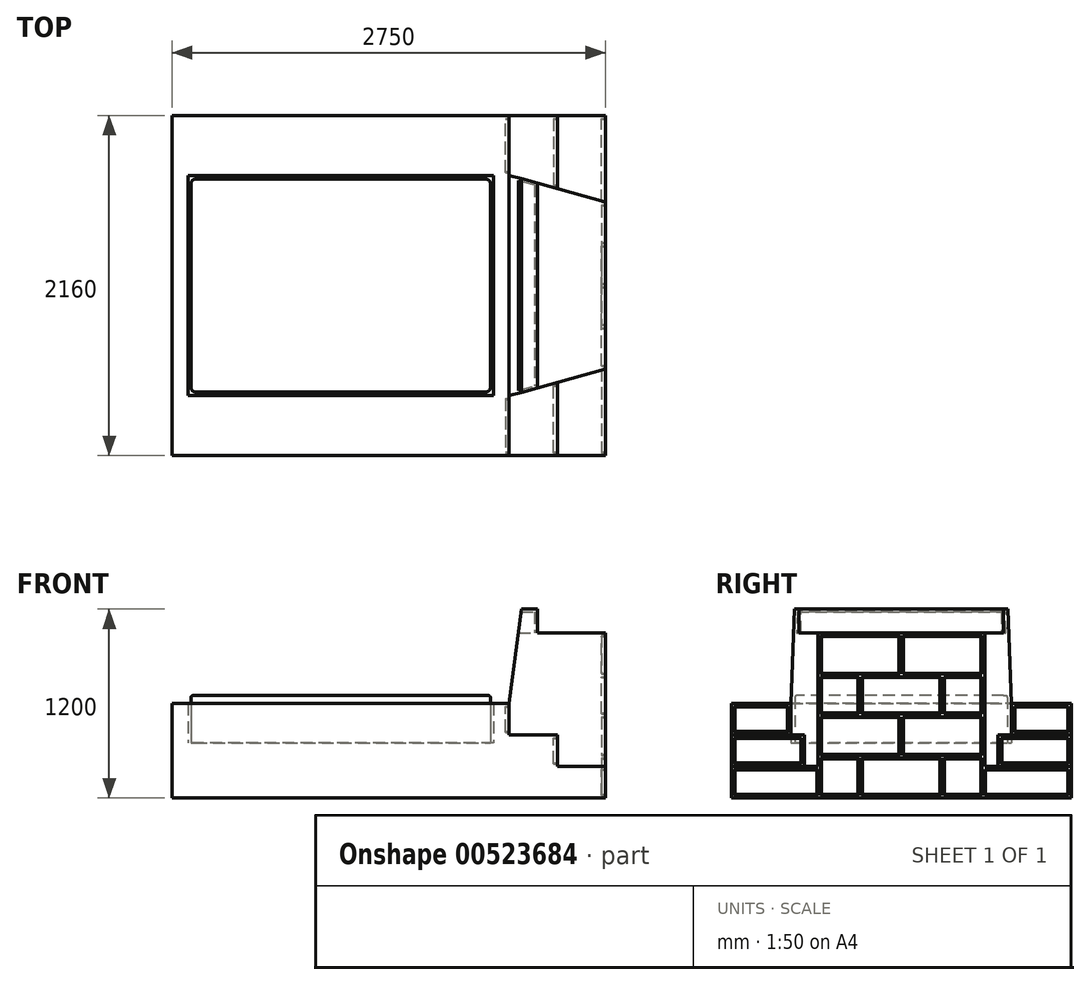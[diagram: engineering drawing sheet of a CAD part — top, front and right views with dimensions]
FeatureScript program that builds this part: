
annotation { "Feature Type Name" : "Feature", "Feature Type Description" : "" }
export const myFeature = defineFeature(function(context is Context, id is Id, definition is map)
    precondition{}
    {
        {
            var Q0;
            Q0=qCreatedBy(makeId("Top.planeOp"),FACE);
            var sketch = newSketch(context, id + "F0", { "sketchPlane" : qUnion([Q0])});
            skLineSegment(sketch, "E0.bottom", {"start": v(1572.5, 1080) * mm, "end": v(-1177.5, 1080) * mm});
            skLineSegment(sketch, "E0.top", {"start": v(1572.5, -1080) * mm, "end": v(-1177.5, -1080) * mm});
            skLineSegment(sketch, "E0.left", {"start": v(1572.5, 1080) * mm, "end": v(1572.5, -1080) * mm});
            skLineSegment(sketch, "E0.right", {"start": v(-1177.5, 1080) * mm, "end": v(-1177.5, -1080) * mm});
            skPoint(sketch, "E0.middle", {"position": v(197.5, 0) * mm});
            skLineSegment(sketch, "E1.bottom", {"start": v(862.5, -700) * mm, "end": v(-1077.5, -700) * mm});
            skLineSegment(sketch, "E1.top", {"start": v(862.5, 700) * mm, "end": v(-1077.5, 700) * mm});
            skLineSegment(sketch, "E1.left", {"start": v(862.5, -700) * mm, "end": v(862.5, 700) * mm});
            skLineSegment(sketch, "E1.right", {"start": v(-1077.5, -700) * mm, "end": v(-1077.5, 700) * mm});
            skPoint(sketch, "E1.middle", {"position": v(-107.5, 0) * mm});
            skLineSegment(sketch, "E2", {"start": v(962.5, 700) * mm, "end": v(962.5, -700) * mm});
            skSolve(sketch);
        }
        {
            var Q0;
            Q0=makeQuery(id+"F0.imprint","IMPRINT",FACE,{"disambiguationData":[TD([[makeQuery(id+"F0.imprint","IMPRINT",EDGE,{"derivedFrom":sQuery(id+"F0.wireOp",EDGE,"E0.bottom")}),1.0]])]});
            extrude(context, id + "F1", {"entities" : qUnion([Q0]), "depth" : 600 * mm, "offsetDistance" : 25 * mm});
        }
        {
            var Q0;
            Q0=makeQuery(id+"F1.opExtrude","CAP_FACE",FACE,{"disambiguationData":[OSD([sQuery(id+"F0.wireOp",EDGE,"E0.bottom"),sQuery(id+"F0.wireOp",EDGE,"E0.top"),sQuery(id+"F0.wireOp",EDGE,"E0.left"),sQuery(id+"F0.wireOp",EDGE,"E0.right"),sQuery(id+"F0.wireOp",EDGE,"E1.bottom"),sQuery(id+"F0.wireOp",EDGE,"E1.top"),sQuery(id+"F0.wireOp",EDGE,"E1.left"),sQuery(id+"F0.wireOp",EDGE,"E1.right")])],"isStart":false});
            var sketch = newSketch(context, id + "F2", { "sketchPlane" : qUnion([Q0])});
            skLineSegment(sketch, "E3", {"start": v(962.5, 1080) * mm, "end": v(962.5, -1080) * mm});
            skLineSegment(sketch, "E4", {"start": v(962.5, -700) * mm, "end": v(1572.5, -530) * mm});
            skLineSegment(sketch, "E5", {"start": v(962.5, 700) * mm, "end": v(1572.5, 530) * mm});
            skLineSegment(sketch, "E6", {"start": v(1267.5, -1080) * mm, "end": v(1267.5, -615) * mm});
            skPoint(sketch, "E6.startSnap0", {"position": v(1267.5, -615) * mm});
            skLineSegment(sketch, "E7", {"start": v(1267.5, 615) * mm, "end": v(1267.5, 1080) * mm});
            skSolve(sketch);
        }
        {
            var Q0;
            {var subQ5=sQuery(id+"F2.wireOp",EDGE,"E7");Q0=makeQuery(id+"F2.imprint","IMPRINT",FACE,{"disambiguationData":[TD([[makeQuery(id+"F2.imprint","IMPRINT",EDGE,{"derivedFrom":subQ5}),1.0]])]});}
            var Q1;
            {var subQ5=sQuery(id+"F2.wireOp",EDGE,"E6");Q1=makeQuery(id+"F2.imprint","IMPRINT",FACE,{"disambiguationData":[TD([[makeQuery(id+"F2.imprint","IMPRINT",EDGE,{"derivedFrom":subQ5}),1.0]])]});}
            extrude(context, id + "F3", {"entities" : qUnion([Q0, Q1]), "operationType" : NewBodyOperationType.REMOVE, "oppositeDirection" : true, "depth" : 200 * mm, "offsetDistance" : 25 * mm});
        }
        {
            var Q0;
            {var subQ3=sQuery(id+"F2.wireOp",EDGE,"E6");Q0=makeQuery(id+"F2.imprint","IMPRINT",FACE,{"disambiguationData":[TD([[makeQuery(id+"F2.imprint","IMPRINT",EDGE,{"derivedFrom":subQ3}),-1.0]])]});}
            var Q1;
            {var subQ3=sQuery(id+"F2.wireOp",EDGE,"E7");Q1=makeQuery(id+"F2.imprint","IMPRINT",FACE,{"disambiguationData":[TD([[makeQuery(id+"F2.imprint","IMPRINT",EDGE,{"derivedFrom":subQ3}),-1.0]])]});}
            extrude(context, id + "F4", {"entities" : qUnion([Q0, Q1]), "operationType" : NewBodyOperationType.REMOVE, "oppositeDirection" : true, "depth" : 400 * mm, "offsetDistance" : 25 * mm});
        }
        {
            var Q0;
            Q0=makeQuery(id+"F1.opExtrude","CAP_FACE",FACE,{"disambiguationData":[OSD([sQuery(id+"F0.wireOp",EDGE,"E0.bottom"),sQuery(id+"F0.wireOp",EDGE,"E0.top"),sQuery(id+"F0.wireOp",EDGE,"E0.left"),sQuery(id+"F0.wireOp",EDGE,"E0.right"),sQuery(id+"F0.wireOp",EDGE,"E1.bottom"),sQuery(id+"F0.wireOp",EDGE,"E1.top"),sQuery(id+"F0.wireOp",EDGE,"E1.left"),sQuery(id+"F0.wireOp",EDGE,"E1.right")])],"isStart":false});
            var sketch = newSketch(context, id + "F5", { "sketchPlane" : qUnion([Q0])});
            skLineSegment(sketch, "E8.0", {"start": v(1572.5, 530) * mm, "end": v(1572.5, -530) * mm});
            skLineSegment(sketch, "E9.0", {"start": v(962.5, 700) * mm, "end": v(1572.5, 530) * mm});
            skLineSegment(sketch, "E10.0", {"start": v(962.5, -700) * mm, "end": v(1572.5, -530) * mm});
            skLineSegment(sketch, "E11.0", {"start": v(862.5, -700) * mm, "end": v(862.5, 700) * mm});
            skLineSegment(sketch, "E12", {"start": v(962.5, 700) * mm, "end": v(962.5, -700) * mm});
            skSolve(sketch);
        }
        {
            var Q0;
            Q0=makeQuery(id+"F5.imprint","IMPRINT",FACE,{"disambiguationData":[TD([[makeQuery(id+"F5.imprint","IMPRINT",EDGE,{"derivedFrom":sQuery(id+"F5.wireOp",EDGE,"E8.0")}),-1.0]])]});
            extrude(context, id + "F6", {"entities" : qUnion([Q0]), "operationType" : NewBodyOperationType.ADD, "depth" : 600 * mm, "offsetDistance" : 25 * mm});
        }
        {
            var Q0;
            Q0=makeQuery(id+"F6.opExtrude","CAP_FACE",FACE,{"disambiguationData":[OSD([sQuery(id+"F5.wireOp",EDGE,"E8.0"),sQuery(id+"F5.wireOp",EDGE,"E9.0"),sQuery(id+"F5.wireOp",EDGE,"E10.0"),sQuery(id+"F5.wireOp",EDGE,"E12")])],"isStart":false});
            var sketch = newSketch(context, id + "F7", { "sketchPlane" : qUnion([Q0])});
            skLineSegment(sketch, "E13.0", {"start": v(1041.49, 677.99) * mm, "end": v(1041.49, -677.99) * mm});
            skLineSegment(sketch, "E14.0", {"start": v(1041.49, -677.99) * mm, "end": v(1572.5, -530) * mm});
            skLineSegment(sketch, "E15.0", {"start": v(1041.49, 677.99) * mm, "end": v(1572.5, 530) * mm});
            skLineSegment(sketch, "E16.0", {"start": v(1572.5, 530) * mm, "end": v(1572.5, -530) * mm});
            skLineSegment(sketch, "E17", {"start": v(1141.49, -650.12) * mm, "end": v(1141.49, 650.12) * mm});
            skSolve(sketch);
        }
        {
            var Q0;
            {var subQ0=sQuery(id+"F7.wireOp",EDGE,"E16.0");Q0=makeQuery(id+"F7.imprint","IMPRINT",FACE,{"disambiguationData":[TD([[makeQuery(id+"F7.imprint","IMPRINT",EDGE,{"derivedFrom":subQ0}),-1.0]])]});}
            extrude(context, id + "F8", {"entities" : qUnion([Q0]), "operationType" : NewBodyOperationType.REMOVE, "oppositeDirection" : true, "depth" : 150 * mm, "offsetDistance" : 25 * mm});
        }
        {
            var Q0;
            Q0=makeQuery(id+"F6.boolean.opBoolean","MERGE",FACE,{"derivedFrom":[makeQuery(id+"F1.opExtrude","SWEPT_FACE",FACE,{"disambiguationData":[OSD([sQuery(id+"F0.wireOp",EDGE,"E0.left")])]}),makeQuery(id+"F6.opExtrude","SWEPT_FACE",FACE,{"disambiguationData":[OSD([sQuery(id+"F5.wireOp",EDGE,"E8.0")])]})]});
            var sketch = newSketch(context, id + "F9", { "sketchPlane" : qUnion([Q0])});
            skLineSegment(sketch, "E18.1", {"start": v(-512, 182) * mm, "end": v(-512, 1032) * mm});
            skLineSegment(sketch, "E18.2", {"start": v(-1062, 182) * mm, "end": v(-1062, 18) * mm});
            skLineSegment(sketch, "E18.3", {"start": v(512, 1032) * mm, "end": v(-512, 1032) * mm});
            skLineSegment(sketch, "E18.4", {"start": v(1062, 18) * mm, "end": v(-1062, 18) * mm});
            skLineSegment(sketch, "E18.5", {"start": v(1062, 182) * mm, "end": v(1062, 18) * mm});
            skLineSegment(sketch, "E18.6", {"start": v(1062, 182) * mm, "end": v(512, 182) * mm});
            skLineSegment(sketch, "E18.7", {"start": v(512, 182) * mm, "end": v(512, 1032) * mm});
            skLineSegment(sketch, "E19", {"start": v(-512, 182) * mm, "end": v(-512, 18) * mm});
            skLineSegment(sketch, "E20", {"start": v(512, 182) * mm, "end": v(512, 18) * mm});
            skLineSegment(sketch, "E21", {"start": v(512, 18) * mm, "end": v(530, 18) * mm});
            skLineSegment(sketch, "E22", {"start": v(530, 18) * mm, "end": v(530, 200) * mm});
            skLineSegment(sketch, "E23", {"start": v(-530, 18) * mm, "end": v(-530, 182) * mm});
            skLineSegment(sketch, "E24", {"start": v(-530, 182) * mm, "end": v(-1062, 182) * mm});
            skLineSegment(sketch, "E25.bottom", {"start": v(-535, 177) * mm, "end": v(-1057, 177) * mm});
            skLineSegment(sketch, "E25.top", {"start": v(-535, 23) * mm, "end": v(-1057, 23) * mm});
            skLineSegment(sketch, "E25.left", {"start": v(-535, 177) * mm, "end": v(-535, 23) * mm});
            skLineSegment(sketch, "E25.right", {"start": v(-1057, 177) * mm, "end": v(-1057, 23) * mm});
            skPoint(sketch, "E25.middle", {"position": v(-796, 100) * mm});
            skPoint(sketch, "E25.middle.positionSnap0", {"position": v(-796, 182) * mm});
            skPoint(sketch, "E25.middle.positionSnap1", {"position": v(-1062, 100) * mm});
            skPoint(sketch, "E25.centerSnap0", {"position": v(-796, 182) * mm});
            skPoint(sketch, "E25.centerSnap1", {"position": v(-1062, 100) * mm});
            skSolve(sketch);
        }
        {
            var Q0;
            {var subQ2=sQuery(id+"F9.wireOp",EDGE,"E18.2");Q0=makeQuery(id+"F9.imprint","IMPRINT",FACE,{"disambiguationData":[TD([[makeQuery(id+"F9.imprint","IMPRINT",EDGE,{"derivedFrom":subQ2}),1.0]])]});}
            extrude(context, id + "F10", {"entities" : qUnion([Q0]), "operationType" : NewBodyOperationType.REMOVE, "oppositeDirection" : true, "depth" : 25 * mm, "offsetDistance" : 25 * mm});
        }
        {
            var Q0;
            Q0=makeQuery(id+"F4.boolean.opBoolean","COPY",FACE,{"derivedFrom":makeQuery(id+"F4.opExtrude","SWEPT_FACE",FACE,{"disambiguationData":[OSD([sQuery(id+"F2.wireOp",EDGE,"E6")])]})});
            var sketch = newSketch(context, id + "F11", { "sketchPlane" : qUnion([Q0])});
            skLineSegment(sketch, "E26.0", {"start": v(-1062, 218) * mm, "end": v(-1062, 382) * mm});
            skLineSegment(sketch, "E26.1", {"start": v(-1062, 218) * mm, "end": v(-633, 218) * mm});
            skLineSegment(sketch, "E26.2", {"start": v(-633, 218) * mm, "end": v(-633, 382) * mm});
            skLineSegment(sketch, "E26.3", {"start": v(-1062, 382) * mm, "end": v(-633, 382) * mm});
            skLineSegment(sketch, "E27.0", {"start": v(-1057, 223) * mm, "end": v(-1057, 377) * mm});
            skLineSegment(sketch, "E27.1", {"start": v(-1057, 223) * mm, "end": v(-638, 223) * mm});
            skLineSegment(sketch, "E27.2", {"start": v(-638, 223) * mm, "end": v(-638, 377) * mm});
            skLineSegment(sketch, "E27.3", {"start": v(-1057, 377) * mm, "end": v(-638, 377) * mm});
            skSolve(sketch);
        }
        {
            var Q0;
            Q0 = qSketchRegion(id + "F11", true);
            extrude(context, id + "F12", {"entities" : qUnion([Q0]), "operationType" : NewBodyOperationType.REMOVE, "oppositeDirection" : true, "depth" : 25 * mm, "offsetDistance" : 25 * mm});
        }
        {
            var Q0;
            {var subQ0=sQuery(id+"F2.wireOp",EDGE,"E3");Q0=makeQuery(id+"F3.boolean.opBoolean","COPY",FACE,{"derivedFrom":makeQuery(id+"F3.opExtrude","SWEPT_FACE",FACE,{"disambiguationData":[OSD([subQ0]),TDD([makeQuery(id+"F2.imprint","IMPRINT",EDGE,{"disambiguationData":[TD([[makeQuery(id+"F2.imprint","INTERSECT",VERTEX,{"derivedFrom":[makeQuery(id+"F1.opExtrude","CAP_EDGE",EDGE,{"disambiguationData":[OSD([sQuery(id+"F0.wireOp",EDGE,"E0.top")])],"isStart":false}),subQ0]}),1.0]])],"derivedFrom":subQ0})])]})});}
            var sketch = newSketch(context, id + "F13", { "sketchPlane" : qUnion([Q0])});
            skLineSegment(sketch, "E28.0", {"start": v(-1062, 418) * mm, "end": v(-1062, 582) * mm});
            skLineSegment(sketch, "E28.1", {"start": v(-718, 418) * mm, "end": v(-1062, 418) * mm});
            skLineSegment(sketch, "E28.2", {"start": v(-718, 418) * mm, "end": v(-718, 582) * mm});
            skLineSegment(sketch, "E28.3", {"start": v(-718, 582) * mm, "end": v(-1062, 582) * mm});
            skLineSegment(sketch, "E29.0", {"start": v(-1057, 423) * mm, "end": v(-1057, 577) * mm});
            skLineSegment(sketch, "E29.1", {"start": v(-723, 423) * mm, "end": v(-1057, 423) * mm});
            skLineSegment(sketch, "E29.2", {"start": v(-723, 423) * mm, "end": v(-723, 577) * mm});
            skLineSegment(sketch, "E29.3", {"start": v(-723, 577) * mm, "end": v(-1057, 577) * mm});
            skSolve(sketch);
        }
        {
            var Q0;
            Q0 = qSketchRegion(id + "F13", true);
            extrude(context, id + "F14", {"entities" : qUnion([Q0]), "operationType" : NewBodyOperationType.REMOVE, "oppositeDirection" : true, "depth" : 25 * mm, "offsetDistance" : 25 * mm});
        }
        {
            var Q0;
            {var subQ1=sQuery(id+"F0.wireOp",EDGE,"E0.left");var subQ2=sQuery(id+"F0.wireOp",EDGE,"E0.bottom");Q0=makeQuery(id+"F10.boolean.opBoolean","SPLIT",FACE,{"disambiguationData":[TD([makeQuery(id+"F1.opExtrude","SWEPT_FACE",FACE,{"disambiguationData":[OSD([subQ2])]})])],"derivedFrom":makeQuery(id+"F6.boolean.opBoolean","MERGE",FACE,{"derivedFrom":[makeQuery(id+"F1.opExtrude","SWEPT_FACE",FACE,{"disambiguationData":[OSD([subQ1])]}),makeQuery(id+"F6.opExtrude","SWEPT_FACE",FACE,{"disambiguationData":[OSD([sQuery(id+"F5.wireOp",EDGE,"E8.0")])]})]})});}
            var sketch = newSketch(context, id + "F15", { "sketchPlane" : qUnion([Q0])});
            skLineSegment(sketch, "E30.bottom", {"start": v(-530, 1050) * mm, "end": v(530, 1050) * mm});
            skLineSegment(sketch, "E30.top", {"start": v(-530, 0) * mm, "end": v(530, 0) * mm});
            skLineSegment(sketch, "E30.left", {"start": v(-530, 1050) * mm, "end": v(-530, 0) * mm});
            skLineSegment(sketch, "E30.right", {"start": v(530, 1050) * mm, "end": v(530, 0) * mm});
            skLineSegment(sketch, "E31.0", {"start": v(512, 1032) * mm, "end": v(512, 18) * mm});
            skLineSegment(sketch, "E31.1", {"start": v(-512, 1032) * mm, "end": v(512, 1032) * mm});
            skLineSegment(sketch, "E31.2", {"start": v(-512, 1032) * mm, "end": v(-512, 18) * mm});
            skLineSegment(sketch, "E31.3", {"start": v(-512, 18) * mm, "end": v(512, 18) * mm});
            skLineSegment(sketch, "E32", {"start": v(0, 778.5) * mm, "end": v(512, 778.5) * mm});
            skLineSegment(sketch, "E33", {"start": v(0, 778.5) * mm, "end": v(0, 1032) * mm});
            skLineSegment(sketch, "E34", {"start": v(512, 1032) * mm, "end": v(512, 778.5) * mm});
            skLineSegment(sketch, "E35.0", {"start": v(9, 787.5) * mm, "end": v(512, 787.5) * mm});
            skLineSegment(sketch, "E35.1", {"start": v(9, 787.5) * mm, "end": v(9, 1032) * mm});
            skLineSegment(sketch, "E36.bottom", {"start": v(507, 792.5) * mm, "end": v(14, 792.5) * mm});
            skLineSegment(sketch, "E36.top", {"start": v(507, 1027) * mm, "end": v(14, 1027) * mm});
            skLineSegment(sketch, "E36.left", {"start": v(507, 792.5) * mm, "end": v(507, 1027) * mm});
            skLineSegment(sketch, "E36.right", {"start": v(14, 792.5) * mm, "end": v(14, 1027) * mm});
            skPoint(sketch, "E36.middle", {"position": v(260.5, 909.75) * mm});
            skPoint(sketch, "E36.middle.positionSnap0", {"position": v(260.5, 787.5) * mm});
            skPoint(sketch, "E36.middle.positionSnap1", {"position": v(9, 909.75) * mm});
            skPoint(sketch, "E36.centerSnap0", {"position": v(260.5, 787.5) * mm});
            skPoint(sketch, "E36.centerSnap1", {"position": v(9, 909.75) * mm});
            skLineSegment(sketch, "E37.MirrorCS", {"start": v(-9, 787.5) * mm, "end": v(-512, 787.5) * mm});
            skPoint(sketch, "E38.MirrorP", {"position": v(-260.5, 909.75) * mm});
            skLineSegment(sketch, "E39.MirrorCS", {"start": v(-507, 1027) * mm, "end": v(-14, 1027) * mm});
            skPoint(sketch, "E40.MirrorP", {"position": v(-260.5, 787.5) * mm});
            skLineSegment(sketch, "E41.MirrorCS", {"start": v(-507, 792.5) * mm, "end": v(-14, 792.5) * mm});
            skLineSegment(sketch, "E42.MirrorCS", {"start": v(-507, 792.5) * mm, "end": v(-507, 1027) * mm});
            skPoint(sketch, "E43.MirrorP", {"position": v(-9, 909.75) * mm});
            skLineSegment(sketch, "E44.MirrorCS", {"start": v(-14, 792.5) * mm, "end": v(-14, 1027) * mm});
            skLineSegment(sketch, "E45.MirrorCS", {"start": v(-9, 787.5) * mm, "end": v(-9, 1032) * mm});
            skPoint(sketch, "E46", {"position": v(0, 525) * mm});
            skLineSegment(sketch, "E47", {"start": v(260.5, 769.5) * mm, "end": v(260.5, 525) * mm});
            skLineSegment(sketch, "E48", {"start": v(-260.5, 525) * mm, "end": v(-260.5, 787.5) * mm});
            skLineSegment(sketch, "E49", {"start": v(-260.5, 525) * mm, "end": v(-512, 525) * mm});
            skLineSegment(sketch, "E50", {"start": v(260.5, 525) * mm, "end": v(512, 525) * mm});
            skLineSegment(sketch, "E51", {"start": v(269.5, 769.5) * mm, "end": v(512, 769.5) * mm});
            skLineSegment(sketch, "E52", {"start": v(512, 534) * mm, "end": v(269.5, 534) * mm});
            skLineSegment(sketch, "E53", {"start": v(269.5, 534) * mm, "end": v(269.5, 769.5) * mm});
            skLineSegment(sketch, "E54", {"start": v(512, 769.5) * mm, "end": v(512, 534) * mm});
            skLineSegment(sketch, "E55.0", {"start": v(507, 764.5) * mm, "end": v(507, 539) * mm});
            skLineSegment(sketch, "E55.1", {"start": v(274.5, 764.5) * mm, "end": v(507, 764.5) * mm});
            skLineSegment(sketch, "E55.2", {"start": v(274.5, 539) * mm, "end": v(274.5, 764.5) * mm});
            skLineSegment(sketch, "E55.3", {"start": v(507, 539) * mm, "end": v(274.5, 539) * mm});
            skLineSegment(sketch, "E56.MirrorCS", {"start": v(-274.5, 539) * mm, "end": v(-274.5, 764.5) * mm});
            skLineSegment(sketch, "E57.MirrorCS", {"start": v(-269.5, 534) * mm, "end": v(-269.5, 769.5) * mm});
            skLineSegment(sketch, "E58.MirrorCS", {"start": v(-269.5, 769.5) * mm, "end": v(-512, 769.5) * mm});
            skLineSegment(sketch, "E59.MirrorCS", {"start": v(-274.5, 764.5) * mm, "end": v(-507, 764.5) * mm});
            skLineSegment(sketch, "E60.MirrorCS", {"start": v(-507, 764.5) * mm, "end": v(-507, 539) * mm});
            skLineSegment(sketch, "E61.MirrorCS", {"start": v(-507, 539) * mm, "end": v(-274.5, 539) * mm});
            skLineSegment(sketch, "E62.MirrorCS", {"start": v(-512, 534) * mm, "end": v(-269.5, 534) * mm});
            skLineSegment(sketch, "E63.MirrorCS", {"start": v(-246.5, 539) * mm, "end": v(-246.5, 764.5) * mm});
            skLineSegment(sketch, "E64.MirrorCS", {"start": v(-251.5, 534) * mm, "end": v(-251.5, 769.5) * mm});
            skLineSegment(sketch, "E65.MirrorCS", {"start": v(251.5, 534) * mm, "end": v(251.5, 769.5) * mm});
            skLineSegment(sketch, "E66.MirrorCS", {"start": v(246.5, 539) * mm, "end": v(246.5, 764.5) * mm});
            skLineSegment(sketch, "E67", {"start": v(-251.5, 769.5) * mm, "end": v(251.5, 769.5) * mm});
            skLineSegment(sketch, "E68", {"start": v(246.5, 764.5) * mm, "end": v(-246.5, 764.5) * mm});
            skLineSegment(sketch, "E69", {"start": v(-246.5, 539) * mm, "end": v(246.5, 539) * mm});
            skLineSegment(sketch, "E70", {"start": v(-251.5, 534) * mm, "end": v(251.5, 534) * mm});
            skLineSegment(sketch, "E71", {"start": v(-260.5, 525) * mm, "end": v(260.5, 525) * mm});
            skLineSegment(sketch, "E72", {"start": v(-246.5, 651.75) * mm, "end": v(246.5, 651.75) * mm});
            skPoint(sketch, "E73.MirrorP", {"position": v(260.5, 516) * mm});
            skLineSegment(sketch, "E74.MirrorCS", {"start": v(507, 276.5) * mm, "end": v(14, 276.5) * mm});
            skPoint(sketch, "E75.MirrorP", {"position": v(-9, 393.75) * mm});
            skLineSegment(sketch, "E76.MirrorCS", {"start": v(-507, 511) * mm, "end": v(-507, 276.5) * mm});
            skPoint(sketch, "E77.MirrorP", {"position": v(-260.5, 393.75) * mm});
            skPoint(sketch, "E78.MirrorP", {"position": v(260.5, 393.75) * mm});
            skLineSegment(sketch, "E79.MirrorCS", {"start": v(-9, 516) * mm, "end": v(-512, 516) * mm});
            skLineSegment(sketch, "E80.MirrorCS", {"start": v(-9, 516) * mm, "end": v(-9, 271.5) * mm});
            skLineSegment(sketch, "E81.MirrorCS", {"start": v(507, 511) * mm, "end": v(507, 276.5) * mm});
            skPoint(sketch, "E82.MirrorP", {"position": v(-260.5, 516) * mm});
            skLineSegment(sketch, "E83.MirrorCS", {"start": v(-512, 271.5) * mm, "end": v(512, 271.5) * mm});
            skPoint(sketch, "E84.MirrorP", {"position": v(9, 393.75) * mm});
            skLineSegment(sketch, "E85.MirrorCS", {"start": v(-507, 511) * mm, "end": v(-14, 511) * mm});
            skLineSegment(sketch, "E86.MirrorCS", {"start": v(9, 516) * mm, "end": v(512, 516) * mm});
            skLineSegment(sketch, "E87.MirrorCS", {"start": v(14, 511) * mm, "end": v(14, 276.5) * mm});
            skLineSegment(sketch, "E88.MirrorCS", {"start": v(-14, 511) * mm, "end": v(-14, 276.5) * mm});
            skLineSegment(sketch, "E89.MirrorCS", {"start": v(507, 511) * mm, "end": v(14, 511) * mm});
            skLineSegment(sketch, "E90.MirrorCS", {"start": v(9, 516) * mm, "end": v(9, 271.5) * mm});
            skLineSegment(sketch, "E91.MirrorCS", {"start": v(-507, 276.5) * mm, "end": v(-14, 276.5) * mm});
            skLineSegment(sketch, "E92", {"start": v(260.5, 393.75) * mm, "end": v(-260.5, 393.75) * mm});
            skLineSegment(sketch, "E93.MirrorCS", {"start": v(-274.5, 23) * mm, "end": v(-507, 23) * mm});
            skLineSegment(sketch, "E94.MirrorCS", {"start": v(-269.5, 253.5) * mm, "end": v(-269.5, 18) * mm});
            skLineSegment(sketch, "E95.MirrorCS", {"start": v(507, 248.5) * mm, "end": v(274.5, 248.5) * mm});
            skLineSegment(sketch, "E96.MirrorCS", {"start": v(274.5, 23) * mm, "end": v(507, 23) * mm});
            skLineSegment(sketch, "E97.MirrorCS", {"start": v(269.5, 253.5) * mm, "end": v(269.5, 18) * mm});
            skLineSegment(sketch, "E98.MirrorCS", {"start": v(507, 23) * mm, "end": v(507, 248.5) * mm});
            skLineSegment(sketch, "E99.MirrorCS", {"start": v(-260.5, 262.5) * mm, "end": v(260.5, 262.5) * mm});
            skLineSegment(sketch, "E100.MirrorCS", {"start": v(-246.5, 248.5) * mm, "end": v(246.5, 248.5) * mm});
            skLineSegment(sketch, "E101.MirrorCS", {"start": v(512, 253.5) * mm, "end": v(269.5, 253.5) * mm});
            skLineSegment(sketch, "E102.MirrorCS", {"start": v(260.5, 262.5) * mm, "end": v(512, 262.5) * mm});
            skLineSegment(sketch, "E103.MirrorCS", {"start": v(246.5, 248.5) * mm, "end": v(246.5, 23) * mm});
            skLineSegment(sketch, "E104.MirrorCS", {"start": v(246.5, 23) * mm, "end": v(-246.5, 23) * mm});
            skLineSegment(sketch, "E105.MirrorCS", {"start": v(-246.5, 248.5) * mm, "end": v(-246.5, 23) * mm});
            skLineSegment(sketch, "E106.MirrorCS", {"start": v(-507, 248.5) * mm, "end": v(-274.5, 248.5) * mm});
            skLineSegment(sketch, "E107.MirrorCS", {"start": v(251.5, 253.5) * mm, "end": v(251.5, 18) * mm});
            skPoint(sketch, "E108.MirrorP", {"position": v(0, 262.5) * mm});
            skLineSegment(sketch, "E109.MirrorCS", {"start": v(-269.5, 18) * mm, "end": v(-512, 18) * mm});
            skLineSegment(sketch, "E110.MirrorCS", {"start": v(-274.5, 248.5) * mm, "end": v(-274.5, 23) * mm});
            skLineSegment(sketch, "E111.MirrorCS", {"start": v(274.5, 248.5) * mm, "end": v(274.5, 23) * mm});
            skLineSegment(sketch, "E112.MirrorCS", {"start": v(512, 18) * mm, "end": v(512, 253.5) * mm});
            skLineSegment(sketch, "E113.MirrorCS", {"start": v(-246.5, 135.75) * mm, "end": v(246.5, 135.75) * mm});
            skLineSegment(sketch, "E114.MirrorCS", {"start": v(-251.5, 253.5) * mm, "end": v(251.5, 253.5) * mm});
            skLineSegment(sketch, "E115.MirrorCS", {"start": v(0, 9) * mm, "end": v(512, 9) * mm});
            skLineSegment(sketch, "E116.MirrorCS", {"start": v(269.5, 18) * mm, "end": v(512, 18) * mm});
            skLineSegment(sketch, "E117.MirrorCS", {"start": v(-251.5, 18) * mm, "end": v(251.5, 18) * mm});
            skLineSegment(sketch, "E118.MirrorCS", {"start": v(260.5, 18) * mm, "end": v(260.5, 262.5) * mm});
            skLineSegment(sketch, "E119.MirrorCS", {"start": v(-260.5, 262.5) * mm, "end": v(-512, 262.5) * mm});
            skLineSegment(sketch, "E120.MirrorCS", {"start": v(-251.5, 253.5) * mm, "end": v(-251.5, 18) * mm});
            skLineSegment(sketch, "E121.MirrorCS", {"start": v(-512, 253.5) * mm, "end": v(-269.5, 253.5) * mm});
            skLineSegment(sketch, "E122.MirrorCS", {"start": v(-507, 23) * mm, "end": v(-507, 248.5) * mm});
            skSolve(sketch);
        }
        {
            var Q0;
            Q0=makeQuery(id+"F15.imprint","IMPRINT",FACE,{"disambiguationData":[TD([[makeQuery(id+"F15.imprint","IMPRINT",EDGE,{"derivedFrom":sQuery(id+"F15.wireOp",EDGE,"E39.MirrorCS")}),1.0]])]});
            var Q1;
            {var subQ1=sQuery(id+"F15.wireOp",EDGE,"E35.0");Q1=makeQuery(id+"F15.imprint","IMPRINT",FACE,{"disambiguationData":[TD([[makeQuery(id+"F15.imprint","IMPRINT",EDGE,{"derivedFrom":subQ1}),1.0]])]});}
            var Q2;
            Q2=makeQuery(id+"F15.imprint","IMPRINT",FACE,{"disambiguationData":[TD([[makeQuery(id+"F15.imprint","IMPRINT",EDGE,{"derivedFrom":sQuery(id+"F15.wireOp",EDGE,"E56.MirrorCS")}),-1.0]])]});
            var Q3;
            Q3=makeQuery(id+"F15.imprint","IMPRINT",FACE,{"disambiguationData":[TD([[makeQuery(id+"F15.imprint","IMPRINT",EDGE,{"derivedFrom":sQuery(id+"F15.wireOp",EDGE,"E64.MirrorCS")}),-1.0]])]});
            var Q4;
            Q4=makeQuery(id+"F15.imprint","IMPRINT",FACE,{"disambiguationData":[TD([[makeQuery(id+"F15.imprint","IMPRINT",EDGE,{"derivedFrom":sQuery(id+"F15.wireOp",EDGE,"E51")}),-1.0]])]});
            var Q5;
            {var subQ7=sQuery(id+"F15.wireOp",EDGE,"E74.MirrorCS");Q5=makeQuery(id+"F15.imprint","IMPRINT",FACE,{"disambiguationData":[TD([[makeQuery(id+"F15.imprint","IMPRINT",EDGE,{"derivedFrom":subQ7}),1.0]])]});}
            var Q6;
            Q6=makeQuery(id+"F15.imprint","IMPRINT",FACE,{"disambiguationData":[TD([[makeQuery(id+"F15.imprint","IMPRINT",EDGE,{"derivedFrom":sQuery(id+"F15.wireOp",EDGE,"E76.MirrorCS")}),-1.0]])]});
            var Q7;
            Q7=makeQuery(id+"F15.imprint","IMPRINT",FACE,{"disambiguationData":[TD([[makeQuery(id+"F15.imprint","IMPRINT",EDGE,{"derivedFrom":sQuery(id+"F15.wireOp",EDGE,"E95.MirrorCS")}),-1.0]])]});
            var Q8;
            {var subQ4=sQuery(id+"F15.wireOp",EDGE,"E100.MirrorCS");Q8=makeQuery(id+"F15.imprint","IMPRINT",FACE,{"disambiguationData":[TD([[makeQuery(id+"F15.imprint","IMPRINT",EDGE,{"derivedFrom":subQ4}),1.0]])]});}
            var Q9;
            Q9=makeQuery(id+"F15.imprint","IMPRINT",FACE,{"disambiguationData":[TD([[makeQuery(id+"F15.imprint","IMPRINT",EDGE,{"derivedFrom":sQuery(id+"F15.wireOp",EDGE,"E93.MirrorCS")}),1.0]])]});
            extrude(context, id + "F16", {"entities" : qUnion([Q0, Q1, Q2, Q3, Q4, Q5, Q6, Q7, Q8, Q9]), "operationType" : NewBodyOperationType.REMOVE, "oppositeDirection" : true, "depth" : 25 * mm, "offsetDistance" : 25 * mm});
        }
        {
            var Q0;
            Q0=makeQuery(id+"F1.opExtrude","CAP_FACE",FACE,{"disambiguationData":[OSD([sQuery(id+"F0.wireOp",EDGE,"E0.bottom"),sQuery(id+"F0.wireOp",EDGE,"E0.top"),sQuery(id+"F0.wireOp",EDGE,"E0.left"),sQuery(id+"F0.wireOp",EDGE,"E0.right"),sQuery(id+"F0.wireOp",EDGE,"E1.bottom"),sQuery(id+"F0.wireOp",EDGE,"E1.top"),sQuery(id+"F0.wireOp",EDGE,"E1.left"),sQuery(id+"F0.wireOp",EDGE,"E1.right")])],"isStart":false});
            var sketch = newSketch(context, id + "F17", { "sketchPlane" : qUnion([Q0])});
            skLineSegment(sketch, "E123.bottom", {"start": v(-1177.5, 1080) * mm, "end": v(2018.1, 1080) * mm});
            skLineSegment(sketch, "E123.top", {"start": v(-1177.5, 0) * mm, "end": v(2018.1, 0) * mm});
            skLineSegment(sketch, "E123.left", {"start": v(-1177.5, 1080) * mm, "end": v(-1177.5, 0) * mm});
            skLineSegment(sketch, "E123.right", {"start": v(2018.1, 1080) * mm, "end": v(2018.1, 0) * mm});
            skSolve(sketch);
        }
        {
            var Q0;
            Q0 = qSketchRegion(id + "F17", true);
            extrude(context, id + "F18", {"entities" : qUnion([Q0]), "operationType" : NewBodyOperationType.REMOVE, "endBound" : BoundingType.THROUGH_ALL, "depth" : 25 * mm, "offsetDistance" : 25 * mm, "hasSecondDirection" : true, "secondDirectionBound" : SecondDirectionBoundingType.THROUGH_ALL, "secondDirectionOppositeDirection" : true, "secondDirectionDepth" : 25 * mm});
        }
        {
            var Q0;
            Q0=makeQuery(id+"F1.opExtrude","SWEPT_BODY",BODY,{"disambiguationData":[OSD([sQuery(id+"F0.wireOp",EDGE,"E0.bottom"),sQuery(id+"F0.wireOp",EDGE,"E0.top"),sQuery(id+"F0.wireOp",EDGE,"E0.left"),sQuery(id+"F0.wireOp",EDGE,"E0.right"),sQuery(id+"F0.wireOp",EDGE,"E1.bottom"),sQuery(id+"F0.wireOp",EDGE,"E1.top"),sQuery(id+"F0.wireOp",EDGE,"E1.left"),sQuery(id+"F0.wireOp",EDGE,"E1.right")])]});
            var Q1;
            {var subQ15=sQuery(id+"F0.wireOp",EDGE,"E0.left");Q1=makeQuery(id+"F18.boolean.opBoolean","COPY",FACE,{"disambiguationData":[TD([makeQuery(id+"F1.opExtrude","SWEPT_FACE",FACE,{"disambiguationData":[OSD([subQ15])]})])],"derivedFrom":makeQuery(id+"F18.opExtrude","SWEPT_FACE",FACE,{"disambiguationData":[OSD([sQuery(id+"F17.wireOp",EDGE,"E123.top")])]})});}
            mirror(context, id + "F19", {"operationType" : NewBodyOperationType.ADD, "entities" : qUnion([Q0]), "mirrorPlane" : qUnion([Q1])});
        }
        {
            var Q0;
            {var subQ0=makeQuery(id+"F1.opExtrude","CAP_FACE",FACE,{"disambiguationData":[OSD([sQuery(id+"F0.wireOp",EDGE,"E0.bottom"),sQuery(id+"F0.wireOp",EDGE,"E0.top"),sQuery(id+"F0.wireOp",EDGE,"E0.left"),sQuery(id+"F0.wireOp",EDGE,"E0.right"),sQuery(id+"F0.wireOp",EDGE,"E1.bottom"),sQuery(id+"F0.wireOp",EDGE,"E1.top"),sQuery(id+"F0.wireOp",EDGE,"E1.left"),sQuery(id+"F0.wireOp",EDGE,"E1.right")])],"isStart":true});Q0=makeQuery(id+"F19.boolean.opBoolean","MERGE",FACE,{"derivedFrom":[subQ0,makeQuery(id+"F19.opPattern","COPY",FACE,{"derivedFrom":subQ0,"instanceName":"1"})]});}
            var sketch = newSketch(context, id + "F20", { "sketchPlane" : qUnion([Q0])});
            skLineSegment(sketch, "E124.bottom", {"start": v(862.5, -700) * mm, "end": v(-1077.5, -700) * mm});
            skLineSegment(sketch, "E124.top", {"start": v(862.5, 700) * mm, "end": v(-1077.5, 700) * mm});
            skLineSegment(sketch, "E124.left", {"start": v(862.5, -700) * mm, "end": v(862.5, 700) * mm});
            skLineSegment(sketch, "E124.right", {"start": v(-1077.5, -700) * mm, "end": v(-1077.5, 700) * mm});
            skSolve(sketch);
        }
        {
            var Q0;
            Q0 = qSketchRegion(id + "F20", true);
            extrude(context, id + "F21", {"entities" : qUnion([Q0]), "operationType" : NewBodyOperationType.ADD, "oppositeDirection" : true, "depth" : 350 * mm, "offsetDistance" : 25 * mm});
        }
        {
            var Q0;
            Q0=makeQuery(id+"F21.opExtrude","CAP_FACE",FACE,{"disambiguationData":[OSD([sQuery(id+"F20.wireOp",EDGE,"E124.bottom"),sQuery(id+"F20.wireOp",EDGE,"E124.top"),sQuery(id+"F20.wireOp",EDGE,"E124.left"),sQuery(id+"F20.wireOp",EDGE,"E124.right")])],"isStart":false});
            var sketch = newSketch(context, id + "F22", { "sketchPlane" : qUnion([Q0])});
            skLineSegment(sketch, "E125.bottom", {"start": v(-1057.5, 675) * mm, "end": v(842.5, 675) * mm});
            skLineSegment(sketch, "E125.top", {"start": v(-1057.5, -675) * mm, "end": v(842.5, -675) * mm});
            skLineSegment(sketch, "E125.left", {"start": v(-1057.5, 675) * mm, "end": v(-1057.5, -675) * mm});
            skLineSegment(sketch, "E125.right", {"start": v(842.5, 675) * mm, "end": v(842.5, -675) * mm});
            skPoint(sketch, "E125.middle", {"position": v(-107.5, 0) * mm});
            skPoint(sketch, "E125.middle.positionSnap0", {"position": v(-1077.5, 0) * mm});
            skPoint(sketch, "E125.middle.positionSnap1", {"position": v(-107.5, -700) * mm});
            skPoint(sketch, "E125.centerSnap0", {"position": v(-1077.5, 0) * mm});
            skPoint(sketch, "E125.centerSnap1", {"position": v(-107.5, -700) * mm});
            skSolve(sketch);
        }
        {
            var Q0;
            Q0=makeQuery(id+"F22.imprint","IMPRINT",FACE,{"disambiguationData":[TD([[makeQuery(id+"F22.imprint","IMPRINT",EDGE,{"derivedFrom":sQuery(id+"F22.wireOp",EDGE,"E125.bottom")}),-1.0]])]});
            extrude(context, id + "F23", {"entities" : qUnion([Q0]), "operationType" : NewBodyOperationType.ADD, "depth" : 300 * mm, "offsetDistance" : 25 * mm});
        }
        {
            var Q0;
            Q0=makeQuery(id+"F23.opExtrude","SWEPT_EDGE",EDGE,{"disambiguationData":[OSD([sQuery(id+"F22.wireOp",EDGE,"E125.bottom"),sQuery(id+"F22.wireOp",EDGE,"E125.left")])]});
            var Q1;
            Q1=makeQuery(id+"F23.opExtrude","SWEPT_EDGE",EDGE,{"disambiguationData":[OSD([sQuery(id+"F22.wireOp",EDGE,"E125.top"),sQuery(id+"F22.wireOp",EDGE,"E125.left")])]});
            var Q2;
            Q2=makeQuery(id+"F23.opExtrude","SWEPT_EDGE",EDGE,{"disambiguationData":[OSD([sQuery(id+"F22.wireOp",EDGE,"E125.bottom"),sQuery(id+"F22.wireOp",EDGE,"E125.right")])]});
            var Q3;
            Q3=makeQuery(id+"F23.opExtrude","SWEPT_EDGE",EDGE,{"disambiguationData":[OSD([sQuery(id+"F22.wireOp",EDGE,"E125.top"),sQuery(id+"F22.wireOp",EDGE,"E125.right")])]});
            fillet(context, id + "F24", {"entities" : qUnion([Q0, Q1, Q2, Q3]), "radius" : 25 * mm, "tangentPropagation" : true, "allowEdgeOverflow" : false});
        }
        {
            var Q0;
            {var subQ0=makeQuery(id+"F6.opExtrude","SWEPT_FACE",FACE,{"disambiguationData":[OSD([sQuery(id+"F5.wireOp",EDGE,"E12")])]});Q0=makeQuery(id+"F19.boolean.opBoolean","MERGE",FACE,{"derivedFrom":[subQ0,makeQuery(id+"F19.opPattern","COPY",FACE,{"derivedFrom":subQ0,"instanceName":"1"})]});}
            var sketch = newSketch(context, id + "F25", { "sketchPlane" : qUnion([Q0])});
            skLineSegment(sketch, "E126.0", {"start": v(-682, 1182) * mm, "end": v(-682, 600) * mm});
            skLineSegment(sketch, "E126.1", {"start": v(-682, 1182) * mm, "end": v(682, 1182) * mm});
            skLineSegment(sketch, "E126.2", {"start": v(682, 1182) * mm, "end": v(682, 600) * mm});
            skLineSegment(sketch, "E127", {"start": v(0, 1182) * mm, "end": v(0, 1050) * mm});
            skPoint(sketch, "E127.endSnap0", {"position": v(0, 1182) * mm});
            skLineSegment(sketch, "E128", {"start": v(-682, 1050) * mm, "end": v(682, 1050) * mm});
            skLineSegment(sketch, "E129", {"start": v(-682, 1032) * mm, "end": v(682, 1032) * mm});
            skSolve(sketch);
        }
        {
            var Q0;
            {var subQ0=sQuery(id+"F2.wireOp",EDGE,"E4");Q0=makeQuery(id+"F6.boolean.opBoolean","MERGE",FACE,{"derivedFrom":[makeQuery(id+"F4.boolean.opBoolean","MERGE",FACE,{"derivedFrom":[makeQuery(id+"F3.boolean.opBoolean","COPY",FACE,{"derivedFrom":makeQuery(id+"F3.opExtrude","SWEPT_FACE",FACE,{"disambiguationData":[OSD([subQ0])]})}),makeQuery(id+"F4.opExtrude","SWEPT_FACE",FACE,{"disambiguationData":[OSD([subQ0])]})]}),makeQuery(id+"F6.opExtrude","SWEPT_FACE",FACE,{"disambiguationData":[OSD([sQuery(id+"F5.wireOp",EDGE,"E10.0")])]})]});}
            var Q1;
            Q1=sQuery(id+"F25.wireOp",VERTEX,"E126.2.start");
            cPlane(context, id + "F26", {"entities" : qUnion([Q0, Q1]), "cplaneType" : CPlaneType.PLANE_POINT, "offset" : 25 * mm, "width" : 150 * mm, "height" : 150 * mm});
        }
        {
            var Q0;
            Q0=qCreatedBy(id+"F26.planeOp",FACE);
            var sketch = newSketch(context, id + "F27", { "sketchPlane" : qUnion([Q0])});
            skPoint(sketch, "E130.0", {"position": v(744.08, 1050) * mm});
            skPoint(sketch, "E131.0", {"position": v(744.08, 1032) * mm});
            skLineSegment(sketch, "E132.0", {"start": v(744.08, 1182) * mm, "end": v(744.08, 600) * mm});
            skLineSegment(sketch, "E133", {"start": v(744.08, 1050) * mm, "end": v(911.2, 1050) * mm});
            skLineSegment(sketch, "E134", {"start": v(911.2, 1050) * mm, "end": v(911.2, 1182) * mm});
            skLineSegment(sketch, "E135", {"start": v(911.2, 1182) * mm, "end": v(744.08, 1182) * mm});
            skSolve(sketch);
        }
        {
            var Q0;
            {var subQ0=sQuery(id+"F2.wireOp",EDGE,"E4");Q0=makeQuery(id+"F19.opPattern","COPY",FACE,{"derivedFrom":makeQuery(id+"F6.boolean.opBoolean","MERGE",FACE,{"derivedFrom":[makeQuery(id+"F4.boolean.opBoolean","MERGE",FACE,{"derivedFrom":[makeQuery(id+"F3.boolean.opBoolean","COPY",FACE,{"derivedFrom":makeQuery(id+"F3.opExtrude","SWEPT_FACE",FACE,{"disambiguationData":[OSD([subQ0])]})}),makeQuery(id+"F4.opExtrude","SWEPT_FACE",FACE,{"disambiguationData":[OSD([subQ0])]})]}),makeQuery(id+"F6.opExtrude","SWEPT_FACE",FACE,{"disambiguationData":[OSD([sQuery(id+"F5.wireOp",EDGE,"E10.0")])]})]}),"instanceName":"1"});}
            var Q1;
            Q1=sQuery(id+"F25.wireOp",VERTEX,"E128.start");
            cPlane(context, id + "F28", {"entities" : qUnion([Q0, Q1]), "cplaneType" : CPlaneType.PLANE_POINT, "offset" : 25 * mm, "width" : 150 * mm, "height" : 150 * mm});
        }
        {
            var Q0;
            Q0=qCreatedBy(id+"F28.planeOp",FACE);
            var sketch = newSketch(context, id + "F29", { "sketchPlane" : qUnion([Q0])});
            skLineSegment(sketch, "E136.0", {"start": v(-744.08, 1182) * mm, "end": v(-744.08, 600) * mm});
            skPoint(sketch, "E137.0", {"position": v(-744.08, 1050) * mm});
            skLineSegment(sketch, "E138", {"start": v(-744.08, 1182) * mm, "end": v(-911.2, 1182) * mm});
            skLineSegment(sketch, "E139", {"start": v(-911.2, 1182) * mm, "end": v(-911.2, 1050) * mm});
            skLineSegment(sketch, "E140", {"start": v(-911.2, 1050) * mm, "end": v(-744.08, 1050) * mm});
            skSolve(sketch);
        }
        {
            var Q1;
            Q1 = qSketchRegion(id + "F29", true);
            var Q2;
            Q2 = qSketchRegion(id + "F27", true);
            loft(context, id + "F30", {"operationType" : NewBodyOperationType.REMOVE, "sheetProfilesArray" : [{ "sheetProfileEntities" : qUnion([Q1]) }, { "sheetProfileEntities" : qUnion([Q2]) }]});
        }
        {
            var Q0;
            Q0=makeQuery(id+"F1.opExtrude","SWEPT_FACE",FACE,{"disambiguationData":[OSD([sQuery(id+"F0.wireOp",EDGE,"E0.top")])]});
            var sketch = newSketch(context, id + "F31", { "sketchPlane" : qUnion([Q0])});
            skPoint(sketch, "E141.0", {"position": v(1041.49, 1200) * mm});
            skPoint(sketch, "E142.0", {"position": v(962.5, 600) * mm});
            skLineSegment(sketch, "E143", {"start": v(1041.49, 1200) * mm, "end": v(962.5, 600) * mm});
            skLineSegment(sketch, "E144", {"start": v(962.5, 600) * mm, "end": v(962.5, 1200) * mm});
            skLineSegment(sketch, "E145", {"start": v(962.5, 1200) * mm, "end": v(1041.49, 1200) * mm});
            skSolve(sketch);
        }
        {
            var Q0;
            Q0 = qSketchRegion(id + "F31", true);
            extrude(context, id + "F32", {"entities" : qUnion([Q0]), "operationType" : NewBodyOperationType.REMOVE, "endBound" : BoundingType.THROUGH_ALL, "oppositeDirection" : true, "depth" : 4279.8 * mm, "offsetDistance" : 25 * mm});
        }
        {
            var Q0;
            Q0=makeQuery(id+"F23.opExtrude","CAP_FACE",FACE,{"disambiguationData":[OSD([sQuery(id+"F22.wireOp",EDGE,"E125.bottom"),sQuery(id+"F22.wireOp",EDGE,"E125.top"),sQuery(id+"F22.wireOp",EDGE,"E125.left"),sQuery(id+"F22.wireOp",EDGE,"E125.right")])],"isStart":false});
            fillet(context, id + "F33", {"entities" : qUnion([Q0]), "radius" : 10 * mm, "tangentPropagation" : true, "allowEdgeOverflow" : false});
        }
    });
